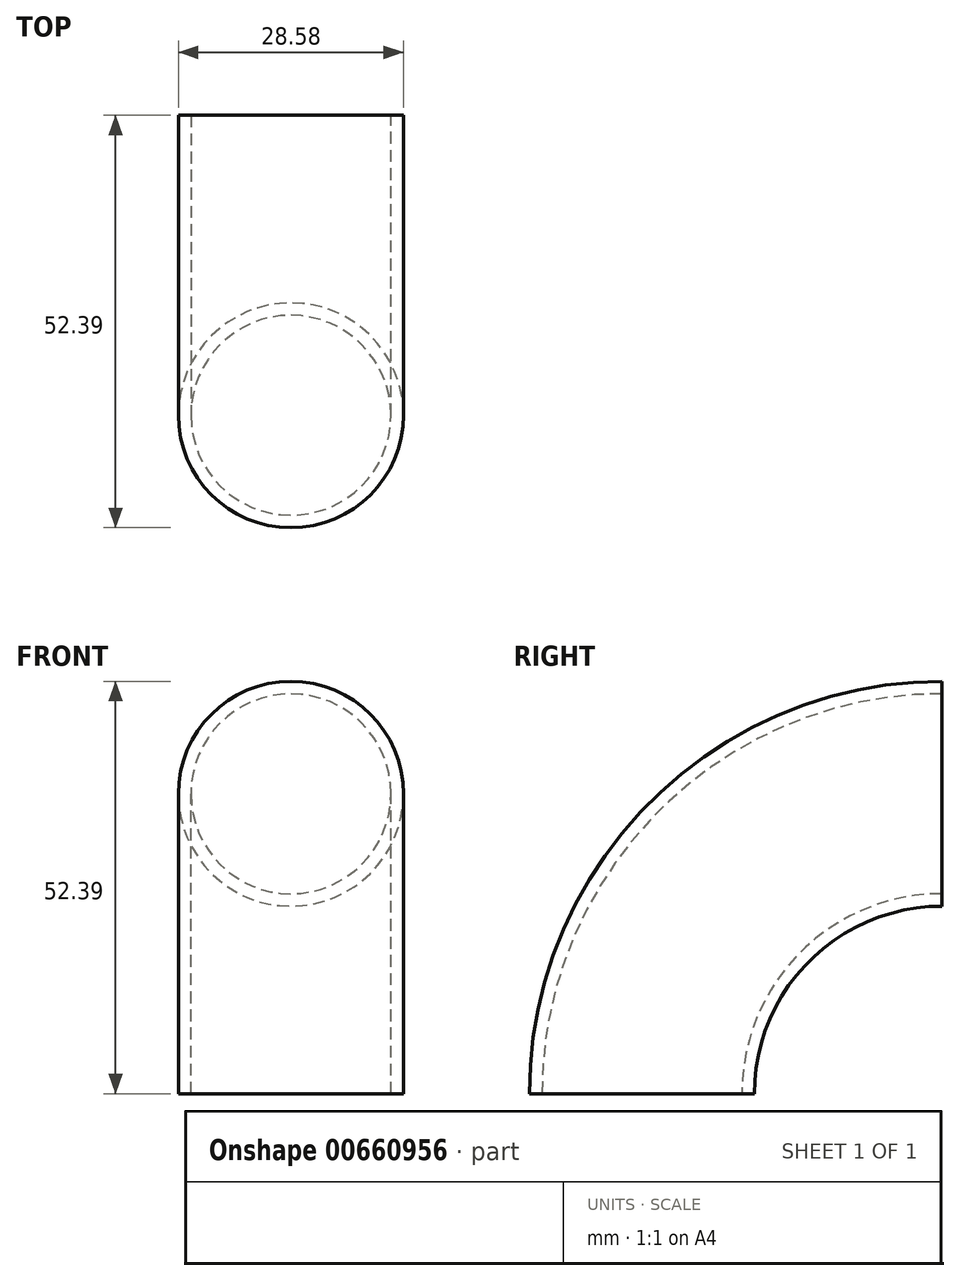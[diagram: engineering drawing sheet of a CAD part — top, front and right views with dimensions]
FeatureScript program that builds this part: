
annotation { "Feature Type Name" : "Feature", "Feature Type Description" : "" }
export const myFeature = defineFeature(function(context is Context, id is Id, definition is map)
    precondition{}
    {
        {
            var Q0;
            Q0=qCreatedBy(makeId("Top.planeOp"),FACE);
            var sketch = newSketch(context, id + "F0", { "sketchPlane" : qUnion([Q0])});
            skLineSegment(sketch, "E0", {"start": v(0, 0) * mm, "end": v(12.7, 0) * mm});
            skCircle(sketch, "E1", {"center": v(0, 0) * mm, "radius": 12.7 * mm});
            skCircle(sketch, "E2.0", {"center": v(0, 0) * mm, "radius": 14.29 * mm});
            skSolve(sketch);
        }
        {
            var Q0;
            Q0=qCreatedBy(makeId("Right.planeOp"),FACE);
            var sketch = newSketch(context, id + "F1", { "sketchPlane" : qUnion([Q0])});
            skLineSegment(sketch, "E3", {"start": v(0, 0) * mm, "end": v(0, 0) * mm});
            skLineSegment(sketch, "E4", {"start": v(0, 0) * mm, "end": v(38.1, 0) * mm});
            skArc(sketch, "E5", {"start": v(0, 0) * mm, "mid": v(11.16, 26.94) * mm, "end": v(38.1, 38.1) * mm});
            skSolve(sketch);
        }
        {
            var Q0;
            Q0=qSketchRegion(id+"F0",true);
            var Q1;
            Q1=sQuery(id+"F1.wireOp",EDGE,"E5");
            sweep(context, id + "F2", {"profiles" : qUnion([Q0]), "path" : qUnion([Q1])});
        }
    });
